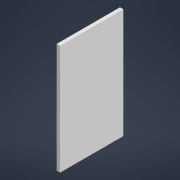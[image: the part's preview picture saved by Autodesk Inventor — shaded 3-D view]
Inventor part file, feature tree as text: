
AUTODESK INVENTOR PART (.ipt)
format: ipt  version: 2022 (Build 260153070, 153G)  size: 88,576 bytes
history: native  units: mm
features: other x1, extrude x1, sketch x1
ambient origin geometry x8: Origin, YZ Plane, XZ Plane, XY Plane, X Axis, Y Axis, Z Axis, Center Point
bodies: Body1 (feature_tree)
feature tree (3):
  other  "Твердое тело1"
  extrude  "Выдавливание1"  Depth=300.0mm
  sketch  "Эскиз2"
